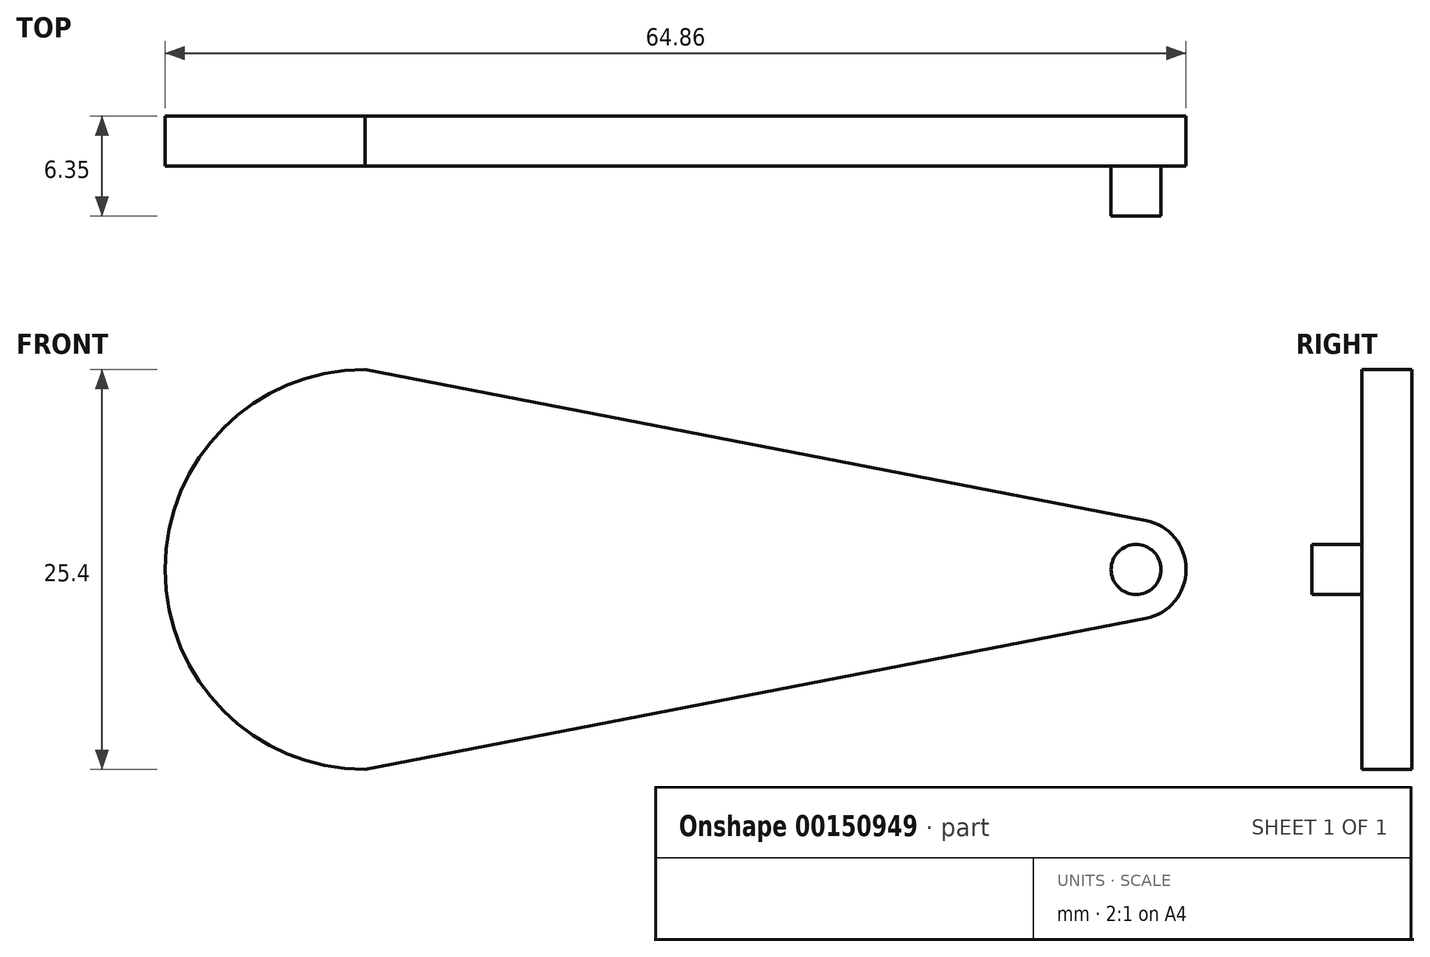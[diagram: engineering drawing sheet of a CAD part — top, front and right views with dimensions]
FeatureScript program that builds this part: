
annotation { "Feature Type Name" : "Feature", "Feature Type Description" : "" }
export const myFeature = defineFeature(function(context is Context, id is Id, definition is map)
    precondition{}
    {
        {
            var Q0;
            Q0=qCreatedBy(makeId("Front.planeOp"),FACE);
            var sketch = newSketch(context, id + "F0", { "sketchPlane" : qUnion([Q0])});
            skArc(sketch, "E0", {"start": v(4.73, 11.79) * mm, "mid": v(-12.7, 0) * mm, "end": v(4.73, -11.79) * mm});
            skArc(sketch, "E1", {"start": v(49.58, -3.12) * mm, "mid": v(52.16, 0) * mm, "end": v(49.58, 3.12) * mm});
            skLineSegment(sketch, "E2", {"start": v(0, 12.7) * mm, "end": v(49.58, 3.12) * mm});
            skLineSegment(sketch, "E3", {"start": v(0, -12.7) * mm, "end": v(49.58, -3.12) * mm});
            skSolve(sketch);
        }
        {
            var Q0;
            {var subQ3=sQuery(id+"F0.wireOp",EDGE,"E1");Q0=makeQuery(id+"F0.imprint","IMPRINT",FACE,{"disambiguationData":[TD([[makeQuery(id+"F0.imprint","IMPRINT",EDGE,{"derivedFrom":subQ3}),1.0]])]});}
            extrude(context, id + "F1", {"entities" : qUnion([Q0]), "depth" : 3.17 * mm});
        }
        {
            var Q0;
            Q0=makeQuery(id+"F1.opExtrude","CAP_FACE",FACE,{"disambiguationData":[OSD([sQuery(id+"F0.wireOp",EDGE,"E0"),sQuery(id+"F0.wireOp",EDGE,"E1"),sQuery(id+"F0.wireOp",EDGE,"E2"),sQuery(id+"F0.wireOp",EDGE,"E3")])],"isStart":false});
            var sketch = newSketch(context, id + "F2", { "sketchPlane" : qUnion([Q0])});
            skCircle(sketch, "E4", {"center": v(48.98, 0) * mm, "radius": 1.59 * mm});
            skSolve(sketch);
        }
        {
            var Q0;
            Q0 = qSketchRegion(id + "F2", true);
            extrude(context, id + "F3", {"entities" : qUnion([Q0]), "operationType" : NewBodyOperationType.ADD, "depth" : 3.17 * mm});
        }
    });
